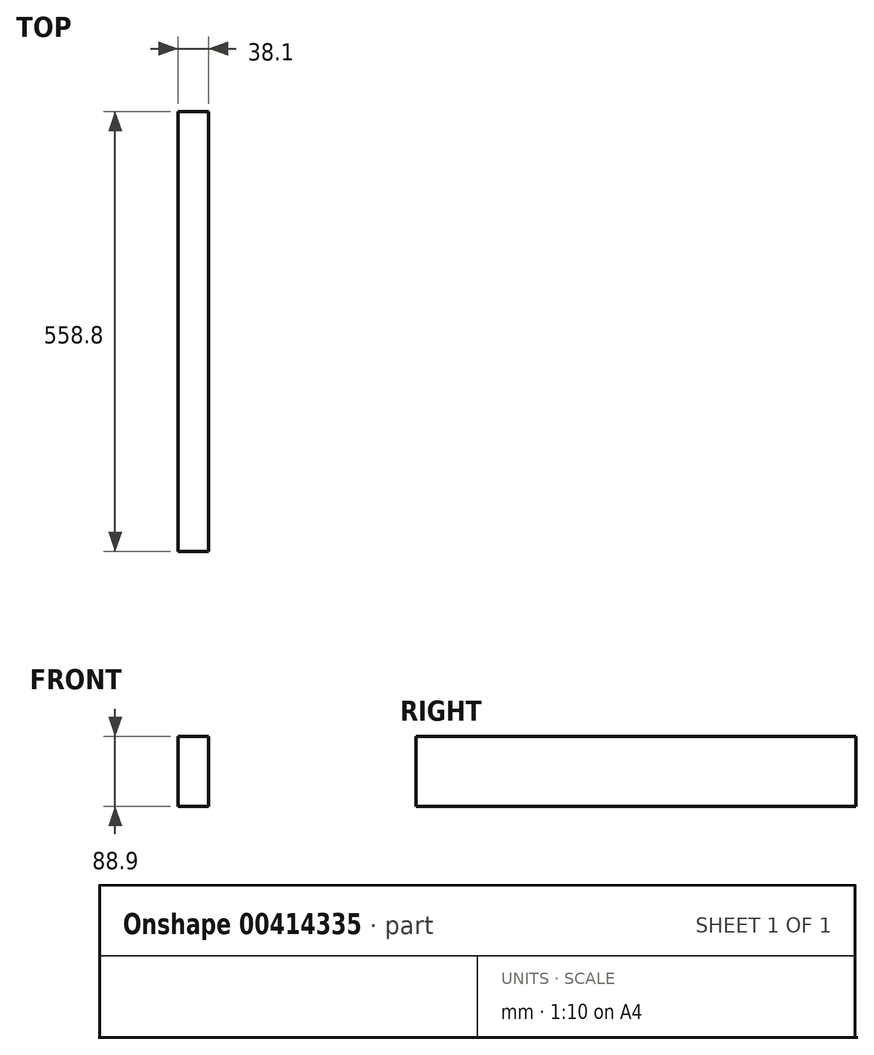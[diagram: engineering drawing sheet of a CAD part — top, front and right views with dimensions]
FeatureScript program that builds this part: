
annotation { "Feature Type Name" : "Feature", "Feature Type Description" : "" }
export const myFeature = defineFeature(function(context is Context, id is Id, definition is map)
    precondition{}
    {
        {
            var Q0;
            Q0=qCreatedBy(makeId("Top.planeOp"),FACE);
            var sketch = newSketch(context, id + "F0", { "sketchPlane" : qUnion([Q0])});
            skLineSegment(sketch, "E0.bottom", {"start": v(-19.05, -279.4) * mm, "end": v(19.05, -279.4) * mm});
            skLineSegment(sketch, "E0.top", {"start": v(-19.05, 279.4) * mm, "end": v(19.05, 279.4) * mm});
            skLineSegment(sketch, "E0.left", {"start": v(-19.05, -279.4) * mm, "end": v(-19.05, 279.4) * mm});
            skLineSegment(sketch, "E0.right", {"start": v(19.05, -279.4) * mm, "end": v(19.05, 279.4) * mm});
            skPoint(sketch, "E0.middle", {"position": v(0, 0) * mm});
            skSolve(sketch);
        }
        {
            var Q0;
            Q0 = qSketchRegion(id + "F0", true);
            extrude(context, id + "F1", {"entities" : qUnion([Q0]), "depth" : 88.9 * mm});
        }
    });
